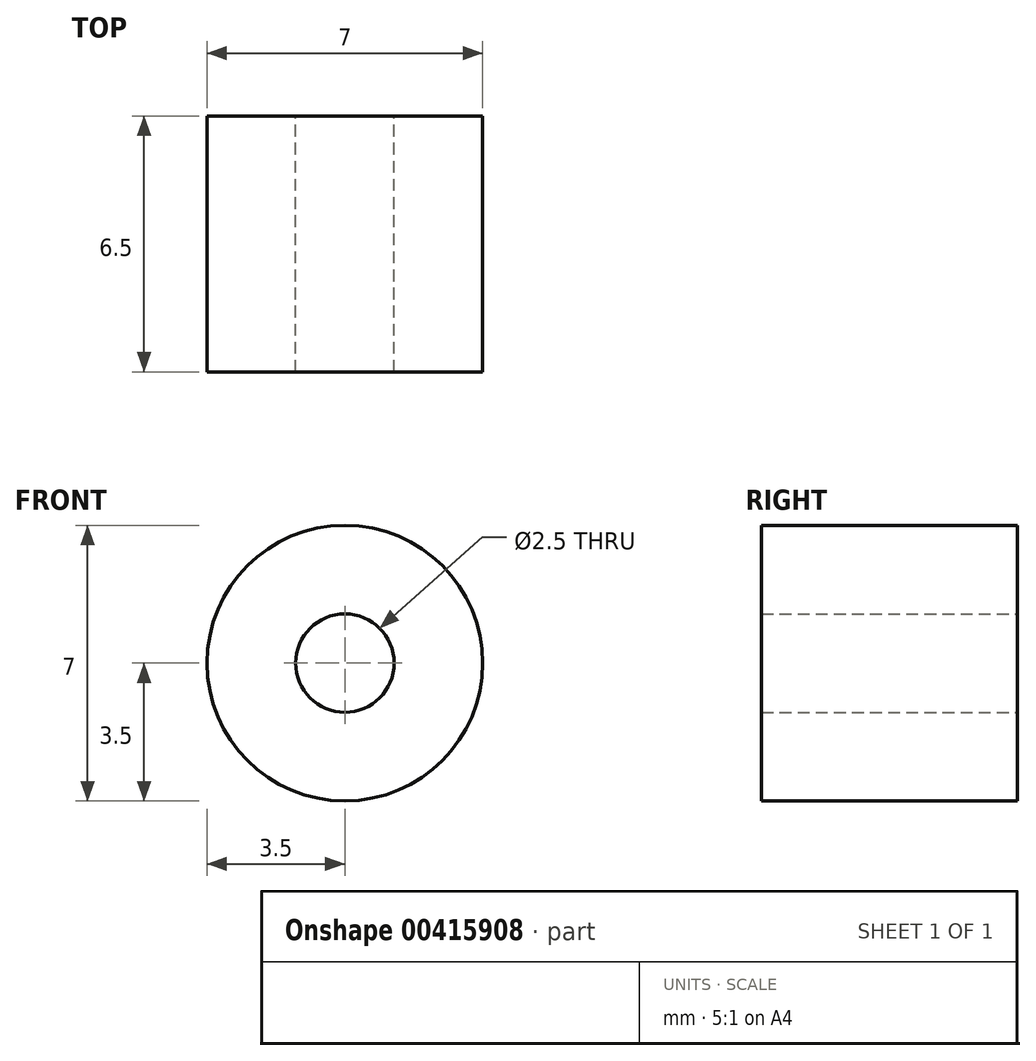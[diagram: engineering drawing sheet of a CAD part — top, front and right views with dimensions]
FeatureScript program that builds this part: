
annotation { "Feature Type Name" : "Feature", "Feature Type Description" : "" }
export const myFeature = defineFeature(function(context is Context, id is Id, definition is map)
    precondition{}
    {
        {
            var Q0;
            Q0=qCreatedBy(makeId("Front.planeOp"),FACE);
            var sketch = newSketch(context, id + "F0", { "sketchPlane" : qUnion([Q0])});
            skCircle(sketch, "E0", {"center": v(0, 0) * mm, "radius": 1.25 * mm});
            skCircle(sketch, "E1", {"center": v(0, 0) * mm, "radius": 3.5 * mm});
            skSolve(sketch);
        }
        {
            var Q0;
            Q0=makeQuery(id+"F0.imprint","IMPRINT",FACE,{"disambiguationData":[TD([[makeQuery(id+"F0.imprint","IMPRINT",EDGE,{"derivedFrom":sQuery(id+"F0.wireOp",EDGE,"E0")}),-1.0]])]});
            extrude(context, id + "F1", {"entities" : qUnion([Q0]), "depth" : 6.5 * mm});
        }
    });
